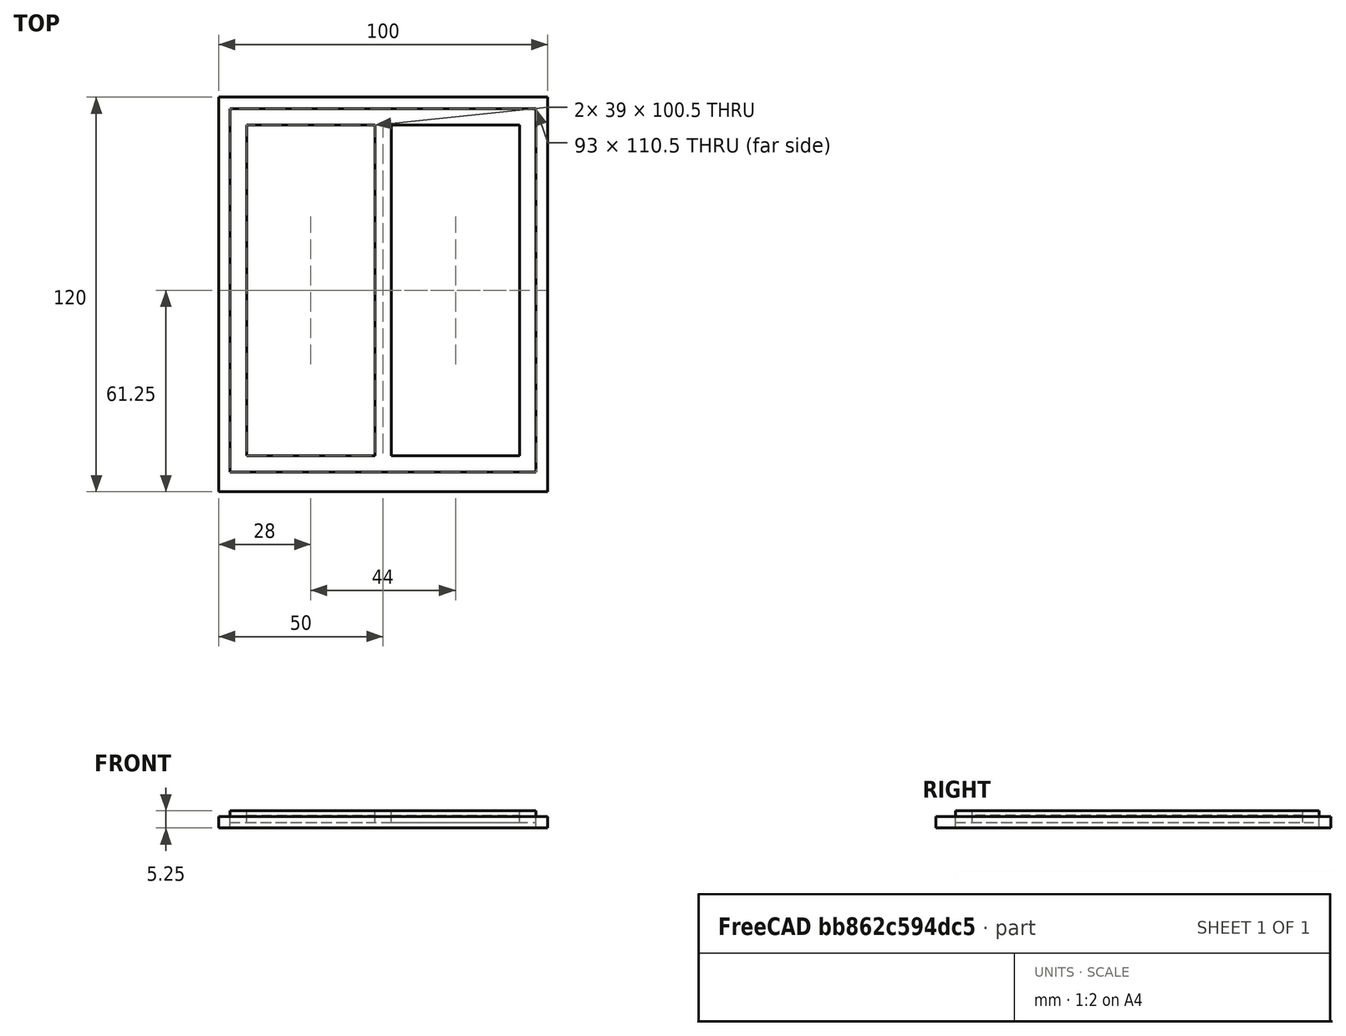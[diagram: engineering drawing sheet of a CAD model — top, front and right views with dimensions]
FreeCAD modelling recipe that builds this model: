
FCSTD DOCUMENT  (FreeCAD 0.16R5636 (Git))
Label: Simple 2-panes window
License: CC-BY 3.0
LicenseURL: http://creativecommons.org/licenses/by/3.0/
objects: Sketcher::SketchObject×1, Mesh::Feature×1, Part::FeaturePython×1
note: 2 computed .brp shape members not serialized (recipe doc carries the construction recipe); baked Part::Feature solids carry a one-line shape summary decoded from their .brp

FEATURE [Sketcher::SketchObject] Sketch
  sketch-geometry (16):
    g0: LineSegment StartX=0 StartY=0 StartZ=0 EndX=100 EndY=0 EndZ=0
    g1: LineSegment StartX=100 StartY=0 StartZ=0 EndX=100 EndY=120 EndZ=0
    g2: LineSegment StartX=100 StartY=120 StartZ=0 EndX=0 EndY=120 EndZ=0
    g3: LineSegment StartX=0 StartY=120 StartZ=0 EndX=0 EndY=0 EndZ=0
    g4: LineSegment StartX=3.5 StartY=116.5 StartZ=0 EndX=96.5 EndY=116.5 EndZ=0
    g5: LineSegment StartX=96.5 StartY=116.5 StartZ=0 EndX=96.5 EndY=6 EndZ=0
    g6: LineSegment StartX=96.5 StartY=6 StartZ=0 EndX=3.5 EndY=6 EndZ=0
    g7: LineSegment StartX=3.5 StartY=6 StartZ=0 EndX=3.5 EndY=116.5 EndZ=0
    g8: LineSegment StartX=8.5 StartY=111.5 StartZ=0 EndX=47.5 EndY=111.5 EndZ=0
    g9: LineSegment StartX=47.5 StartY=111.5 StartZ=0 EndX=47.5 EndY=11 EndZ=0
    g10: LineSegment StartX=47.5 StartY=11 StartZ=0 EndX=8.5 EndY=11 EndZ=0
    g11: LineSegment StartX=8.5 StartY=11 StartZ=0 EndX=8.5 EndY=111.5 EndZ=0
    g12: LineSegment StartX=52.5 StartY=111.5 StartZ=0 EndX=91.5 EndY=111.5 EndZ=0
    g13: LineSegment StartX=91.5 StartY=111.5 StartZ=0 EndX=91.5 EndY=11 EndZ=0
    g14: LineSegment StartX=91.5 StartY=11 StartZ=0 EndX=52.5 EndY=11 EndZ=0
    g15: LineSegment StartX=52.5 StartY=11 StartZ=0 EndX=52.5 EndY=111.5 EndZ=0
  constraints (48):
    c: Coincident(g0,g1)
    c: Coincident(g1,g2)
    c: Coincident(g2,g3)
    c: Coincident(g3,g0)
    c: Horizontal(g0)
    c: Horizontal(g2)
    c: Vertical(g1)
    c: Vertical(g3)
    c: DistanceX(g0) = 0
    c: DistanceY(g0) = 0
    c: DistanceX(g2,g1) = 100
    c: DistanceY(g1,g0) = -120
    c: Coincident(g4,g5)
    c: Coincident(g5,g6)
    c: Coincident(g6,g7)
    c: Coincident(g7,g4)
    c: Horizontal(g4)
    c: Horizontal(g6)
    c: Vertical(g5)
    c: Vertical(g7)
    c: Coincident(g8,g9)
    c: Coincident(g9,g10)
    c: Coincident(g10,g11)
    c: Coincident(g11,g8)
    c: Horizontal(g8)
    c: Horizontal(g10)
    c: Vertical(g9)
    c: Vertical(g11)
    c: Coincident(g12,g13)
    c: Coincident(g13,g14)
    c: Coincident(g14,g15)
    c: Coincident(g15,g12)
    c: Horizontal(g12)
    c: Horizontal(g14)
    c: Vertical(g13)
    c: Vertical(g15)
    c: DistanceY(g8,g4) = 5
    c: DistanceY(g12,g8) = 0
    c: DistanceX(g4,g8) = 5
    c: DistanceX(g4,g12) = -5
    c: DistanceY(g6,g10) = 5
    c: DistanceY(g9,g14) = 0
    c: DistanceY(g4,g2) = 3.5
    c: DistanceX(g4,g2) = -3.5
    c: DistanceX(g4,g1) = 3.5
    c: DistanceY(g-1,g6) = 6
    c: DistanceX(g8,g12) = 5
    c: Equal(g8,g12)
FEATURE [Mesh::Feature] latch2  label="Latch"
  Placement = pos=(49.1438,64.0559,5.25) rot=(0,0,1;0rad)
FEATURE [Part::FeaturePython] Window  # WARN: FeaturePython — macro-defined, semantics opaque (R4)
  Base = -> Sketch
  Fixtures = -> [latch2]
  WindowParts = Fixed frame | Frame | Wire0,Wire1,Wire2,Wire3 | -3.5 | 0 | Mobile frame | Frame | Wire1,Wire2,Wire3 | 3.5 | 1.75 | Left glass | Glass panel | Wire2 | .3 | 3.5 | Right glass | Glass panel | Wire3 | .3 | 3.5
